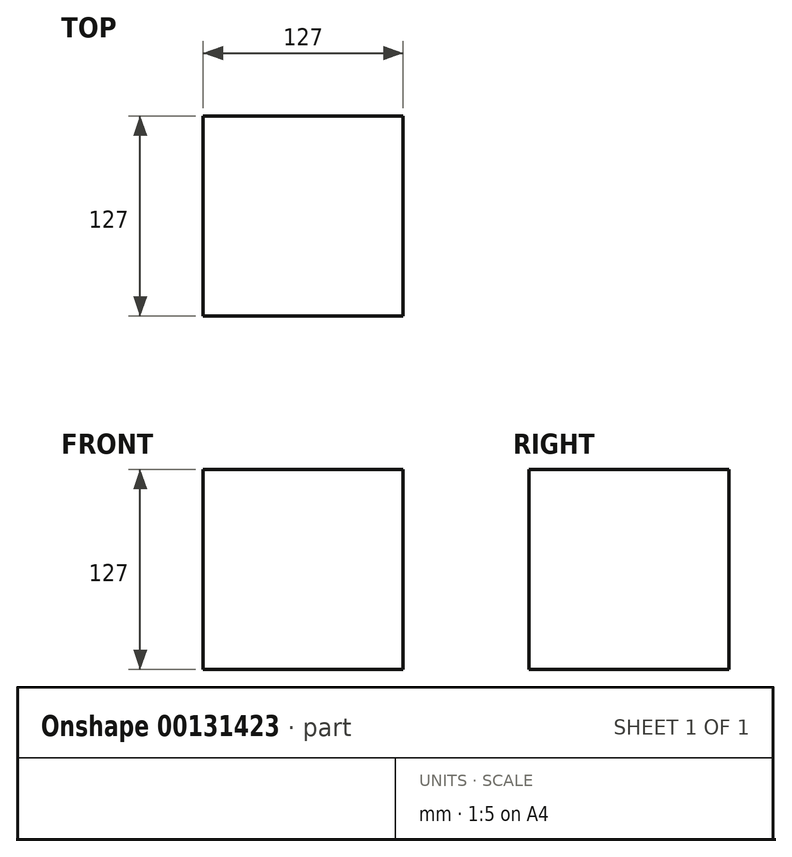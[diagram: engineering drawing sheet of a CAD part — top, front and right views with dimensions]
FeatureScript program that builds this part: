
annotation { "Feature Type Name" : "Feature", "Feature Type Description" : "" }
export const myFeature = defineFeature(function(context is Context, id is Id, definition is map)
    precondition{}
    {
        {
            var Q0;
            Q0=qCreatedBy(makeId("Front.planeOp"),FACE);
            var sketch = newSketch(context, id + "F0", { "sketchPlane" : qUnion([Q0])});
            skLineSegment(sketch, "E0.bottom", {"start": v(63.5, 63.5) * mm, "end": v(-63.5, 63.5) * mm});
            skLineSegment(sketch, "E0.top", {"start": v(63.5, -63.5) * mm, "end": v(-63.5, -63.5) * mm});
            skLineSegment(sketch, "E0.left", {"start": v(63.5, 63.5) * mm, "end": v(63.5, -63.5) * mm});
            skLineSegment(sketch, "E0.right", {"start": v(-63.5, 63.5) * mm, "end": v(-63.5, -63.5) * mm});
            skPoint(sketch, "E0.middle", {"position": v(0, 0) * mm});
            skSolve(sketch);
        }
        {
            var Q0;
            Q0=makeQuery(id+"F0.imprint","IMPRINT",FACE,{"disambiguationData":[TD([[makeQuery(id+"F0.imprint","IMPRINT",EDGE,{"derivedFrom":sQuery(id+"F0.wireOp",EDGE,"E0.bottom")}),1.0]])]});
            extrude(context, id + "F1", {"entities" : qUnion([Q0]), "depth" : 127 * mm});
        }
    });
